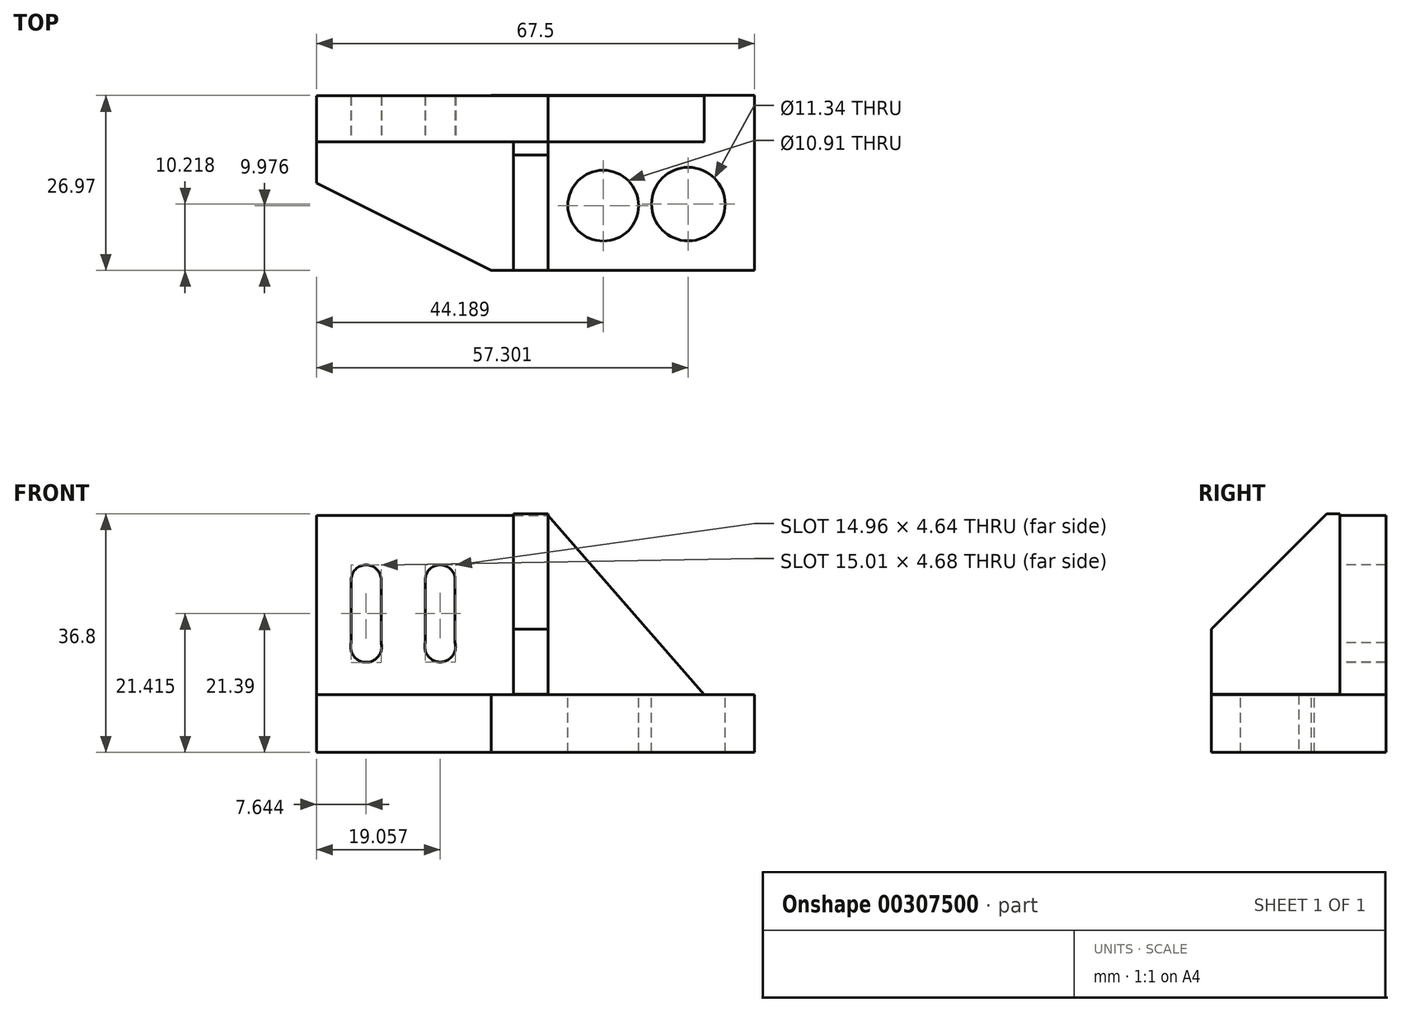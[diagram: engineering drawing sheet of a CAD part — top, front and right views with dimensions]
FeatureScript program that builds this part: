
annotation { "Feature Type Name" : "Feature", "Feature Type Description" : "" }
export const myFeature = defineFeature(function(context is Context, id is Id, definition is map)
    precondition{}
    {
        {
            var Q0;
            Q0=qCreatedBy(makeId("Front.planeOp"),FACE);
            var sketch = newSketch(context, id + "F0", { "sketchPlane" : qUnion([Q0])});
            skLineSegment(sketch, "E0.bottom", {"start": v(-35.7, 0) * mm, "end": v(0, 0) * mm});
            skLineSegment(sketch, "E0.top", {"start": v(-35.7, 36.54) * mm, "end": v(0, 36.54) * mm});
            skLineSegment(sketch, "E0.left", {"start": v(-35.7, 0) * mm, "end": v(-35.7, 36.54) * mm});
            skLineSegment(sketch, "E0.right", {"start": v(0, 0) * mm, "end": v(0, 36.54) * mm});
            skLineSegment(sketch, "E1", {"start": v(0, 0) * mm, "end": v(31.8, 0) * mm});
            skLineSegment(sketch, "E2", {"start": v(31.8, 0) * mm, "end": v(0, 36.54) * mm});
            skSolve(sketch);
        }
        {
            var Q0;
            Q0 = qSketchRegion(id + "F0", true);
            extrude(context, id + "F1", {"entities" : qUnion([Q0]), "oppositeDirection" : true, "depth" : 7.11 * mm});
        }
        {
            var Q0;
            Q0=qCreatedBy(makeId("Top.planeOp"),FACE);
            var sketch = newSketch(context, id + "F2", { "sketchPlane" : qUnion([Q0])});
            skLineSegment(sketch, "E3.bottom", {"start": v(-8.74, 7.16) * mm, "end": v(31.8, 7.16) * mm});
            skLineSegment(sketch, "E3.top", {"start": v(-8.74, -19.8) * mm, "end": v(31.8, -19.8) * mm});
            skLineSegment(sketch, "E3.left", {"start": v(-8.74, 7.16) * mm, "end": v(-8.74, -19.8) * mm});
            skLineSegment(sketch, "E3.right", {"start": v(31.8, 7.16) * mm, "end": v(31.8, -19.8) * mm});
            skLineSegment(sketch, "E4.bottom", {"start": v(-35.7, 6.92) * mm, "end": v(-8.74, 6.92) * mm});
            skLineSegment(sketch, "E4.top", {"start": v(-35.7, -6.31) * mm, "end": v(-8.74, -6.31) * mm});
            skLineSegment(sketch, "E4.left", {"start": v(-35.7, 6.92) * mm, "end": v(-35.7, -6.31) * mm});
            skLineSegment(sketch, "E4.right", {"start": v(-8.74, 6.92) * mm, "end": v(-8.74, -6.31) * mm});
            skLineSegment(sketch, "E5", {"start": v(-35.7, -6.31) * mm, "end": v(-8.74, -19.8) * mm});
            skSolve(sketch);
        }
        {
            var Q0;
            Q0 = qSketchRegion(id + "F2", true);
            extrude(context, id + "F3", {"entities" : qUnion([Q0]), "operationType" : NewBodyOperationType.ADD, "depth" : 8.9 * mm});
        }
        {
            var Q0;
            Q0=qCreatedBy(makeId("Front.planeOp"),FACE);
            var sketch = newSketch(context, id + "F4", { "sketchPlane" : qUnion([Q0])});
            skLineSegment(sketch, "E6.bottom", {"start": v(0, 36.8) * mm, "end": v(-5.31, 36.8) * mm});
            skLineSegment(sketch, "E6.top", {"start": v(0, 8.96) * mm, "end": v(-5.31, 8.96) * mm});
            skLineSegment(sketch, "E6.left", {"start": v(0, 36.8) * mm, "end": v(0, 8.96) * mm});
            skLineSegment(sketch, "E6.right", {"start": v(-5.31, 36.8) * mm, "end": v(-5.31, 8.96) * mm});
            skSolve(sketch);
        }
        {
            var Q0;
            Q0 = qSketchRegion(id + "F4", true);
            extrude(context, id + "F5", {"entities" : qUnion([Q0]), "operationType" : NewBodyOperationType.ADD, "depth" : 19.8 * mm});
        }
        {
            var Q0;
            Q0=makeQuery(id+"F5.opExtrude","CAP_EDGE",EDGE,{"disambiguationData":[OSD([sQuery(id+"F4.wireOp",EDGE,"E6.bottom")])],"isStart":false});
            chamfer(context, id + "F6", {"entities" : qUnion([Q0]), "width" : 17.78 * mm, "tangentPropagation" : true});
        }
        {
            var Q0;
            Q0=qCreatedBy(makeId("Front.planeOp"),FACE);
            var sketch = newSketch(context, id + "F7", { "sketchPlane" : qUnion([Q0])});
            skLineSegment(sketch, "E7", {"start": v(-30.35, 26.59) * mm, "end": v(-30.35, 16.88) * mm});
            skLineSegment(sketch, "E8", {"start": v(-30.35, 16.88) * mm, "end": v(-30.35, 26.59) * mm});
            skLineSegment(sketch, "E9", {"start": v(-25.74, 26.59) * mm, "end": v(-25.74, 16.88) * mm});
            skLineSegment(sketch, "E10", {"start": v(-18.94, 16.88) * mm, "end": v(-18.94, 26.59) * mm});
            skLineSegment(sketch, "E11", {"start": v(-14.33, 26.59) * mm, "end": v(-14.33, 16.88) * mm});
            skArc(sketch, "E12", {"start": v(-25.74, 26.59) * mm, "mid": v(-28.05, 28.9) * mm, "end": v(-30.35, 26.59) * mm});
            skArc(sketch, "E13", {"start": v(-30.35, 16.88) * mm, "mid": v(-28.05, 13.88) * mm, "end": v(-25.74, 16.88) * mm});
            skArc(sketch, "E14", {"start": v(-18.94, 16.88) * mm, "mid": v(-16.63, 13.93) * mm, "end": v(-14.33, 16.88) * mm});
            skArc(sketch, "E15", {"start": v(-14.33, 26.59) * mm, "mid": v(-16.63, 28.9) * mm, "end": v(-18.94, 26.59) * mm});
            skSolve(sketch);
        }
        {
            var Q0;
            Q0 = qSketchRegion(id + "F7", true);
            extrude(context, id + "F8", {"entities" : qUnion([Q0]), "operationType" : NewBodyOperationType.REMOVE, "oppositeDirection" : true, "depth" : 25.4 * mm});
        }
        {
            var Q0;
            Q0=makeQuery(id+"F3.opExtrude","CAP_FACE",FACE,{"disambiguationData":[OSD([sQuery(id+"F2.wireOp",EDGE,"E3.bottom"),sQuery(id+"F2.wireOp",EDGE,"E3.top"),sQuery(id+"F2.wireOp",EDGE,"E3.left"),sQuery(id+"F2.wireOp",EDGE,"E3.right"),sQuery(id+"F2.wireOp",EDGE,"E4.bottom"),sQuery(id+"F2.wireOp",EDGE,"E4.left"),sQuery(id+"F2.wireOp",EDGE,"E5")])],"isStart":false});
            var sketch = newSketch(context, id + "F9", { "sketchPlane" : qUnion([Q0])});
            skCircle(sketch, "E16", {"center": v(8.5, -9.83) * mm, "radius": 5.46 * mm});
            skCircle(sketch, "E17", {"center": v(21.61, -9.6) * mm, "radius": 5.67 * mm});
            skSolve(sketch);
        }
        {
            var Q0;
            Q0 = qSketchRegion(id + "F9", true);
            extrude(context, id + "F10", {"entities" : qUnion([Q0]), "operationType" : NewBodyOperationType.REMOVE, "oppositeDirection" : true, "depth" : 25.4 * mm});
        }
    });
